# Revit family: LRTG Clearform
name_source: partatom
category: Lighting Fixtures
units: mm (PartAtom-declared; Revit-internal decimal feet)

## family parameters
Always vertical = Yes
Cut with Voids When Loaded = No
Host = Ceiling
Light Source = Yes
OmniClass Number = 23.80.70.11
OmniClass Title = Luminaries for Internal Lighting
Part Type = Normal
Room Calculation Point = No
Round Connector Dimension = Use Diameter
Shared = No

## types (9) — shared parameters
Assembly Code = D5020200
Color Filter = 16777215
Description = LED Recessed Type CLEARFORM
Dimming Lamp Color Temperature Shift = <None>
Emit Shape Visible in Rendering = No
Housing Finish = Metal - Viscor - White
Lamp = LED
Lens Finish = Polycarbonate - Viscor - Frosted
Manufacturer = VISIONEERING by VISCOR
Model = CLEARFORM
Tilt Angle = 90.00°
URL = https://www.viscor.com
Voltage = 120 V

## per-type parameters (varying)
| type | Apparent Load | Emit from Rectangle Length | Emit from Rectangle Width | End | Lamp Wattage | Length | Photometric Web File | Reflector Width | Width |
| LRTG1X4-LED840K040LUNV-P94 | 31 VA | 3' - 11 3/4" | 0' - 11 3/4" | 1' - 11 7/8" | 31 VA | 3' - 11 3/4" | LRTG1X4-LED840K040LUNV-P94.ies | 0' - 5 7/8" | 0' - 11 3/4" |
| LRTG20X60-LED840K050LUNV-P94 | 37 VA | 4' - 11 3/4" | 1' - 7 3/4" | 2' - 5 7/8" | 37 VA | 4' - 11 3/4" | LRTG20X60-LED840K050LUNV-P94.ies | 0' - 9 7/8" | 1' - 7 3/4" |
| LRTG2X2-LED840K037LUNV-P94 | 34 VA | 1' - 11 3/4" | 1' - 11 3/4" | 0' - 11 7/8" | 34 VA | 1' - 11 3/4" | LRTG2X2-LED840K037LUNV-P94.IES | 0' - 11 7/8" | 1' - 11 3/4" |
| LRTG2X2-LED840K050LUNV-P94 | 38 VA | 1' - 11 3/4" | 1' - 11 3/4" | 0' - 11 7/8" | 38 VA | 1' - 11 3/4" | LRTG2x2-LED840K050LUNV-P94.IES | 0' - 11 7/8" | 1' - 11 3/4" |
| LRTG2X4-LED840K040LUNV-P94 | 30 VA | 3' - 11 3/4" | 1' - 11 3/4" | 1' - 11 7/8" | 30 VA | 3' - 11 3/4" | LRTG2x4-LED840K040LUNV-P94.IES | 0' - 11 7/8" | 1' - 11 3/4" |
| LRTG2x4-LED840K050LUNV-P94 | 39 VA | 3' - 11 3/4" | 1' - 11 3/4" | 1' - 11 7/8" | 39 VA | 3' - 11 3/4" | LRTG2X4-LED840K050LUNV-P94.ies | 0' - 11 7/8" | 1' - 11 3/4" |
| LRTG2x4-LED840K074LUNV-P94 | 58 VA | 3' - 11 3/4" | 1' - 11 3/4" | 1' - 11 7/8" | 58 VA | 3' - 11 3/4" | LRTG2X4-LED840K074LUNV-P94.ies | 0' - 11 7/8" | 1' - 11 3/4" |
| LRTG2x4-LED840K092LUNV-P94 | 79 VA | 3' - 11 3/4" | 1' - 11 3/4" | 1' - 11 7/8" | 79 VA | 3' - 11 3/4" | LRTG2X4-LED840K092LUNV-P94.ies | 0' - 11 7/8" | 1' - 11 3/4" |
| LRTG30x30-LED840K040LUNV-P94 | 37 VA | 2' - 5 3/4" | 2' - 5 3/4" | 1' - 2 7/8" | 37 VA | 2' - 5 3/4" | LRTG30x30-LED840K040LUNV-P94.IES | 1' - 2 7/8" | 2' - 5 3/4" |

## geometry (parser evidence)
native form markers: Sweep x5
no freeform markers — native parametric forms only
